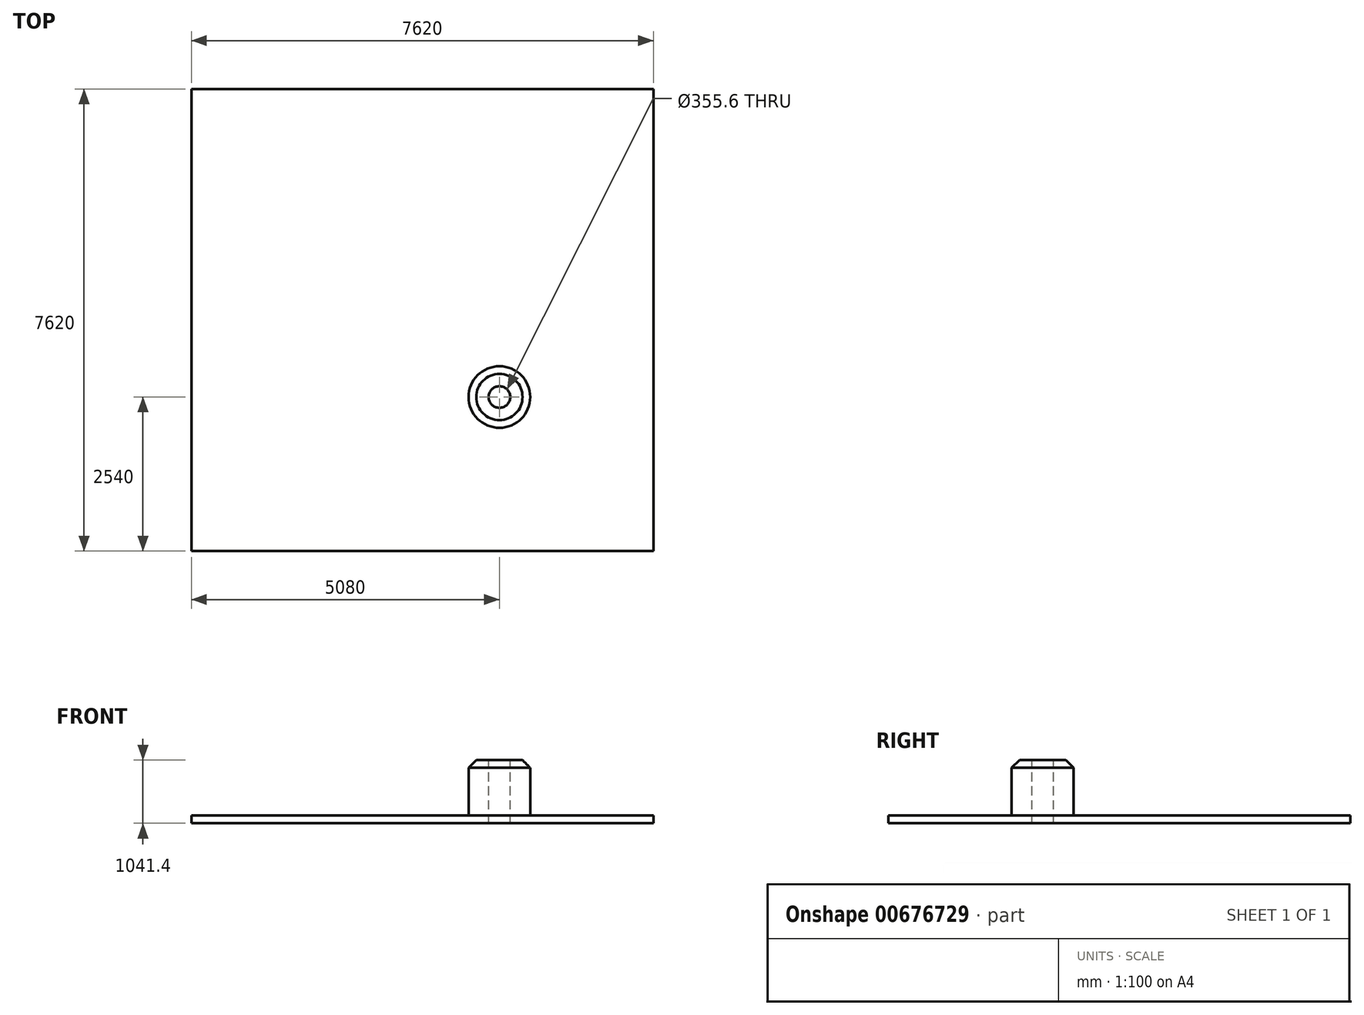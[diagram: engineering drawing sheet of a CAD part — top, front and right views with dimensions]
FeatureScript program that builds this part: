
annotation { "Feature Type Name" : "Feature", "Feature Type Description" : "" }
export const myFeature = defineFeature(function(context is Context, id is Id, definition is map)
    precondition{}
    {
        {
            var Q0;
            Q0=qCreatedBy(makeId("Top.planeOp"),FACE);
            var sketch = newSketch(context, id + "F0", { "sketchPlane" : qUnion([Q0])});
            skLineSegment(sketch, "E0.bottom", {"start": v(3810, 3810) * mm, "end": v(-3810, 3810) * mm});
            skLineSegment(sketch, "E0.top", {"start": v(3810, -3810) * mm, "end": v(-3810, -3810) * mm});
            skLineSegment(sketch, "E0.left", {"start": v(3810, 3810) * mm, "end": v(3810, -3810) * mm});
            skLineSegment(sketch, "E0.right", {"start": v(-3810, 3810) * mm, "end": v(-3810, -3810) * mm});
            skPoint(sketch, "E0.middle", {"position": v(0, 0) * mm});
            skSolve(sketch);
        }
        {
            var Q0;
            Q0=makeQuery(id+"F0.imprint","IMPRINT",FACE,{"disambiguationData":[TD([[makeQuery(id+"F0.imprint","IMPRINT",EDGE,{"derivedFrom":sQuery(id+"F0.wireOp",EDGE,"E0.bottom")}),1.0]])]});
            extrude(context, id + "F1", {"entities" : qUnion([Q0]), "depth" : 127 * mm, "offsetDistance" : 25.4 * mm});
        }
        {
            var Q0;
            Q0=makeQuery(id+"F1.opExtrude","CAP_FACE",FACE,{"disambiguationData":[OSD([sQuery(id+"F0.wireOp",EDGE,"E0.bottom"),sQuery(id+"F0.wireOp",EDGE,"E0.top"),sQuery(id+"F0.wireOp",EDGE,"E0.left"),sQuery(id+"F0.wireOp",EDGE,"E0.right")])],"isStart":false});
            var sketch = newSketch(context, id + "F2", { "sketchPlane" : qUnion([Q0])});
            skCircle(sketch, "E1", {"center": v(1270, -1270) * mm, "radius": 508 * mm});
            skSolve(sketch);
        }
        {
            var Q0;
            Q0=makeQuery(id+"F2.imprint","IMPRINT",FACE,{"disambiguationData":[TD([[makeQuery(id+"F2.imprint","IMPRINT",EDGE,{"derivedFrom":sQuery(id+"F2.wireOp",EDGE,"E1")}),1.0]])]});
            extrude(context, id + "F3", {"entities" : qUnion([Q0]), "operationType" : NewBodyOperationType.ADD, "depth" : 914.4 * mm, "offsetDistance" : 25.4 * mm});
        }
        {
            var Q0;
            Q0=makeQuery(id+"F3.opExtrude","CAP_EDGE",EDGE,{"disambiguationData":[OSD([sQuery(id+"F2.wireOp",EDGE,"E1")])],"isStart":false});
            var Q1;
            Q1=makeQuery(id+"F3.opExtrude","CAP_EDGE",EDGE,{"disambiguationData":[OSD([sQuery(id+"F2.wireOp",EDGE,"E1")])],"isStart":true});
            chamfer(context, id + "F4", {"entities" : qUnion([Q0, Q1]), "width" : 127 * mm, "tangentPropagation" : true});
        }
        {
            var Q0;
            Q0=makeQuery(id+"F3.opExtrude","CAP_FACE",FACE,{"disambiguationData":[OSD([sQuery(id+"F2.wireOp",EDGE,"E1")])],"isStart":false});
            var sketch = newSketch(context, id + "F5", { "sketchPlane" : qUnion([Q0])});
            skCircle(sketch, "E2", {"center": v(1270, -1270) * mm, "radius": 177.8 * mm});
            skSolve(sketch);
        }
        {
            var Q0;
            Q0=makeQuery(id+"F5.imprint","IMPRINT",FACE,{"disambiguationData":[TD([[makeQuery(id+"F5.imprint","IMPRINT",EDGE,{"derivedFrom":sQuery(id+"F5.wireOp",EDGE,"E2")}),1.0]])]});
            extrude(context, id + "F6", {"entities" : qUnion([Q0]), "operationType" : NewBodyOperationType.REMOVE, "endBound" : BoundingType.THROUGH_ALL, "oppositeDirection" : true, "depth" : 25.4 * mm, "offsetDistance" : 25.4 * mm});
        }
    });
